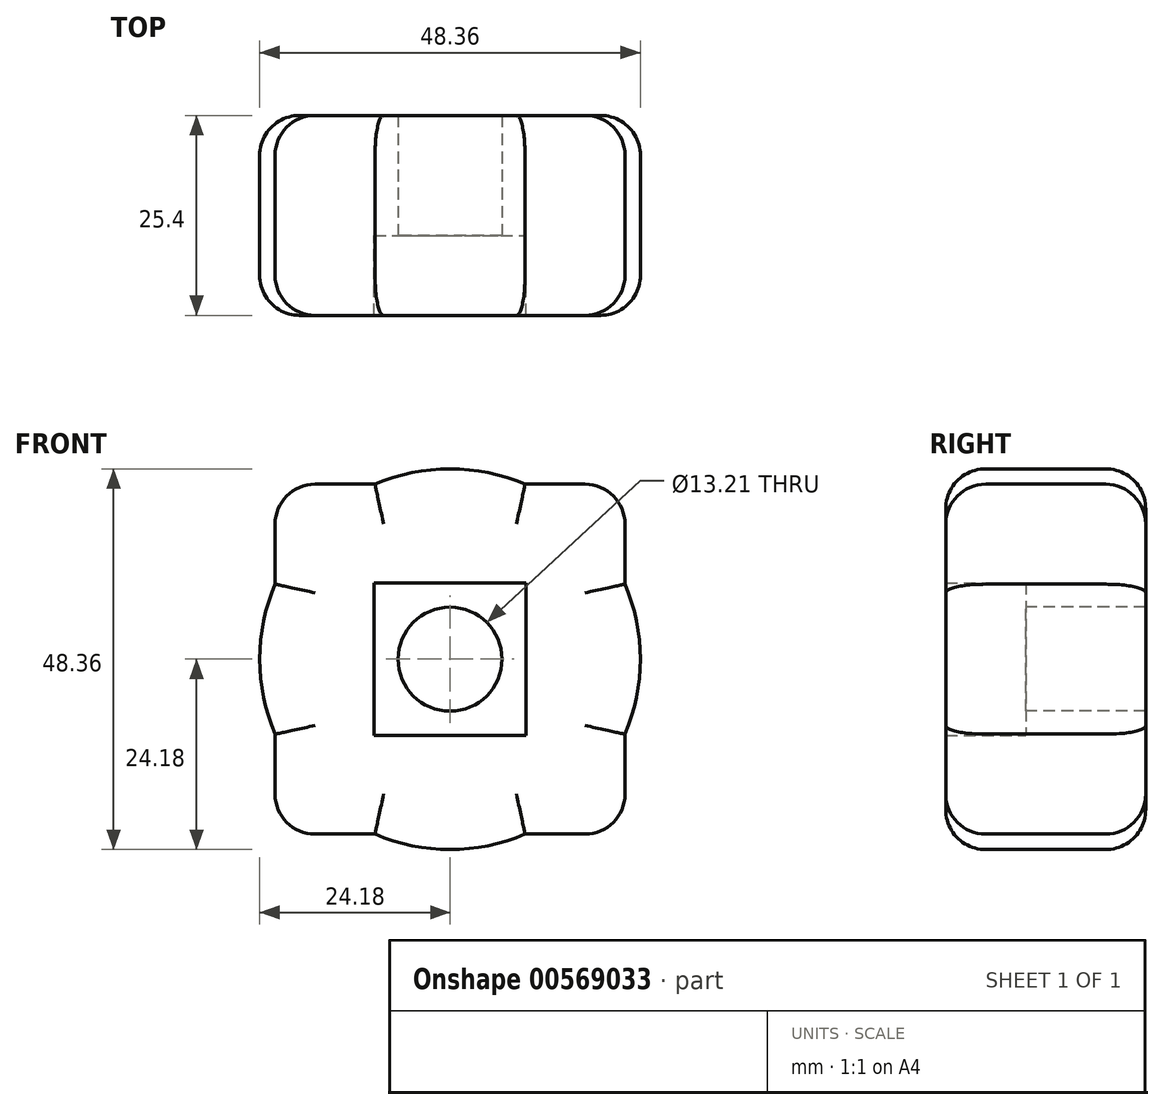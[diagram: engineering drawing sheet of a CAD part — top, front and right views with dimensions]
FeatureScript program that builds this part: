
annotation { "Feature Type Name" : "Feature", "Feature Type Description" : "" }
export const myFeature = defineFeature(function(context is Context, id is Id, definition is map)
    precondition{}
    {
        {
            var Q0;
            Q0=qCreatedBy(makeId("Front.planeOp"),FACE);
            var sketch = newSketch(context, id + "F0", { "sketchPlane" : qUnion([Q0])});
            skLineSegment(sketch, "E0.bottom", {"start": v(-22.22, -22.23) * mm, "end": v(-9.53, -22.23) * mm});
            skLineSegment(sketch, "E0.top", {"start": v(-22.22, 22.23) * mm, "end": v(-9.53, 22.23) * mm});
            skLineSegment(sketch, "E0.left", {"start": v(-22.22, -22.23) * mm, "end": v(-22.22, -9.53) * mm});
            skLineSegment(sketch, "E0.right", {"start": v(22.23, -22.23) * mm, "end": v(22.23, -9.53) * mm});
            skArc(sketch, "E1", {"start": v(9.53, 22.22) * mm, "mid": v(0, 24.18) * mm, "end": v(-9.53, 22.22) * mm});
            skLineSegment(sketch, "E2.trimOffspring", {"start": v(-22.22, 9.53) * mm, "end": v(-22.22, 22.23) * mm});
            skLineSegment(sketch, "E3.trimOffspring", {"start": v(9.53, 22.23) * mm, "end": v(22.23, 22.23) * mm});
            skLineSegment(sketch, "E4.trimOffspring", {"start": v(22.23, 9.53) * mm, "end": v(22.23, 22.23) * mm});
            skArc(sketch, "E5.trimOffspring", {"start": v(-22.22, 9.53) * mm, "mid": v(-24.18, 0) * mm, "end": v(-22.22, -9.53) * mm});
            skArc(sketch, "E6.trimOffspring", {"start": v(22.23, -9.52) * mm, "mid": v(24.18, 0) * mm, "end": v(22.23, 9.53) * mm});
            skArc(sketch, "E7.trimOffspring", {"start": v(-9.53, -22.22) * mm, "mid": v(0, -24.18) * mm, "end": v(9.52, -22.23) * mm});
            skLineSegment(sketch, "E8.trimOffspring", {"start": v(9.53, -22.23) * mm, "end": v(22.23, -22.23) * mm});
            skLineSegment(sketch, "E9.bottom", {"start": v(-9.65, 9.7) * mm, "end": v(9.65, 9.7) * mm});
            skLineSegment(sketch, "E9.top", {"start": v(-9.65, -9.7) * mm, "end": v(9.65, -9.7) * mm});
            skLineSegment(sketch, "E9.left", {"start": v(-9.65, 9.7) * mm, "end": v(-9.65, -9.7) * mm});
            skLineSegment(sketch, "E9.right", {"start": v(9.65, 9.7) * mm, "end": v(9.65, -9.7) * mm});
            skSolve(sketch);
        }
        {
            var Q0;
            Q0 = qSketchRegion(id + "F0", true);
            extrude(context, id + "F1", {"entities" : qUnion([Q0]), "depth" : 25.4 * mm, "offsetDistance" : 25.4 * mm});
        }
        {
            var Q0;
            Q0=makeQuery(id+"F0.imprint","IMPRINT",FACE,{"disambiguationData":[TD([[makeQuery(id+"F0.imprint","IMPRINT",EDGE,{"derivedFrom":sQuery(id+"F0.wireOp",EDGE,"E9.bottom")}),-1.0]])]});
            extrude(context, id + "F2", {"entities" : qUnion([Q0]), "operationType" : NewBodyOperationType.ADD, "depth" : 15.24 * mm, "offsetDistance" : 25.4 * mm});
        }
        {
            var Q0;
            Q0=makeQuery(id+"F2.opExtrude","CAP_FACE",FACE,{"disambiguationData":[OSD([sQuery(id+"F0.wireOp",EDGE,"E9.bottom"),sQuery(id+"F0.wireOp",EDGE,"E9.top"),sQuery(id+"F0.wireOp",EDGE,"E9.left"),sQuery(id+"F0.wireOp",EDGE,"E9.right")])],"isStart":false});
            var sketch = newSketch(context, id + "F3", { "sketchPlane" : qUnion([Q0])});
            skCircle(sketch, "E10", {"center": v(0, 0) * mm, "radius": 6.6 * mm});
            skSolve(sketch);
        }
        {
            var Q0;
            Q0 = qSketchRegion(id + "F3", true);
            extrude(context, id + "F4", {"entities" : qUnion([Q0]), "operationType" : NewBodyOperationType.REMOVE, "oppositeDirection" : true, "depth" : 127 * mm, "offsetDistance" : 25.4 * mm});
        }
        {
            var Q0;
            Q0=makeQuery(id+"F1.opExtrude","SWEPT_EDGE",EDGE,{"disambiguationData":[OSD([sQuery(id+"F0.wireOp",EDGE,"E0.bottom"),sQuery(id+"F0.wireOp",EDGE,"E0.left")])]});
            var Q1;
            Q1=makeQuery(id+"F1.opExtrude","SWEPT_EDGE",EDGE,{"disambiguationData":[OSD([sQuery(id+"F0.wireOp",EDGE,"E0.top"),sQuery(id+"F0.wireOp",EDGE,"E2.trimOffspring")])]});
            var Q2;
            Q2=makeQuery(id+"F1.opExtrude","SWEPT_EDGE",EDGE,{"disambiguationData":[OSD([sQuery(id+"F0.wireOp",EDGE,"E3.trimOffspring"),sQuery(id+"F0.wireOp",EDGE,"E4.trimOffspring")])]});
            var Q3;
            Q3=makeQuery(id+"F1.opExtrude","SWEPT_EDGE",EDGE,{"disambiguationData":[OSD([sQuery(id+"F0.wireOp",EDGE,"E0.right"),sQuery(id+"F0.wireOp",EDGE,"E8.trimOffspring")])]});
            fillet(context, id + "F5", {"entities" : qUnion([Q0, Q1, Q2, Q3]), "radius" : 5.08 * mm, "tangentPropagation" : true, "allowEdgeOverflow" : false});
        }
        {
            var Q0;
            Q0=makeQuery(id+"F1.opExtrude","CAP_EDGE",EDGE,{"disambiguationData":[OSD([sQuery(id+"F0.wireOp",EDGE,"E0.bottom")])],"isStart":false});
            var Q1;
            Q1=makeQuery(id+"F1.opExtrude","CAP_EDGE",EDGE,{"disambiguationData":[OSD([sQuery(id+"F0.wireOp",EDGE,"E0.bottom")])],"isStart":true});
            var Q2;
            Q2=makeQuery(id+"F1.opExtrude","CAP_EDGE",EDGE,{"disambiguationData":[OSD([sQuery(id+"F0.wireOp",EDGE,"E0.top")])],"isStart":true});
            var Q3;
            Q3=makeQuery(id+"F1.opExtrude","CAP_EDGE",EDGE,{"disambiguationData":[OSD([sQuery(id+"F0.wireOp",EDGE,"E2.trimOffspring")])],"isStart":false});
            var Q4;
            Q4=makeQuery(id+"F1.opExtrude","CAP_EDGE",EDGE,{"disambiguationData":[OSD([sQuery(id+"F0.wireOp",EDGE,"E4.trimOffspring")])],"isStart":false});
            var Q5;
            Q5=makeQuery(id+"F1.opExtrude","CAP_EDGE",EDGE,{"disambiguationData":[OSD([sQuery(id+"F0.wireOp",EDGE,"E0.right")])],"isStart":false});
            var Q6;
            Q6=makeQuery(id+"F1.opExtrude","CAP_EDGE",EDGE,{"disambiguationData":[OSD([sQuery(id+"F0.wireOp",EDGE,"E8.trimOffspring")])],"isStart":true});
            var Q7;
            Q7=makeQuery(id+"F1.opExtrude","CAP_EDGE",EDGE,{"disambiguationData":[OSD([sQuery(id+"F0.wireOp",EDGE,"E3.trimOffspring")])],"isStart":true});
            var Q8;
            Q8=makeQuery(id+"F1.opExtrude","CAP_EDGE",EDGE,{"disambiguationData":[OSD([sQuery(id+"F0.wireOp",EDGE,"E7.trimOffspring")])],"isStart":false});
            var Q9;
            Q9=makeQuery(id+"F1.opExtrude","CAP_EDGE",EDGE,{"disambiguationData":[OSD([sQuery(id+"F0.wireOp",EDGE,"E7.trimOffspring")])],"isStart":true});
            var Q10;
            Q10=makeQuery(id+"F1.opExtrude","CAP_EDGE",EDGE,{"disambiguationData":[OSD([sQuery(id+"F0.wireOp",EDGE,"E1")])],"isStart":true});
            var Q11;
            Q11=makeQuery(id+"F1.opExtrude","CAP_EDGE",EDGE,{"disambiguationData":[OSD([sQuery(id+"F0.wireOp",EDGE,"E1")])],"isStart":false});
            var Q12;
            Q12=makeQuery(id+"F1.opExtrude","CAP_EDGE",EDGE,{"disambiguationData":[OSD([sQuery(id+"F0.wireOp",EDGE,"E6.trimOffspring")])],"isStart":false});
            var Q13;
            Q13=makeQuery(id+"F1.opExtrude","CAP_EDGE",EDGE,{"disambiguationData":[OSD([sQuery(id+"F0.wireOp",EDGE,"E6.trimOffspring")])],"isStart":true});
            var Q14;
            Q14=makeQuery(id+"F1.opExtrude","CAP_EDGE",EDGE,{"disambiguationData":[OSD([sQuery(id+"F0.wireOp",EDGE,"E5.trimOffspring")])],"isStart":true});
            var Q15;
            Q15=makeQuery(id+"F1.opExtrude","CAP_EDGE",EDGE,{"disambiguationData":[OSD([sQuery(id+"F0.wireOp",EDGE,"E5.trimOffspring")])],"isStart":false});
            fillet(context, id + "F6", {"entities" : qUnion([Q0, Q1, Q2, Q3, Q4, Q5, Q6, Q7, Q8, Q9, Q10, Q11, Q12, Q13, Q14, Q15]), "radius" : 5.08 * mm, "tangentPropagation" : true, "allowEdgeOverflow" : false});
        }
    });
